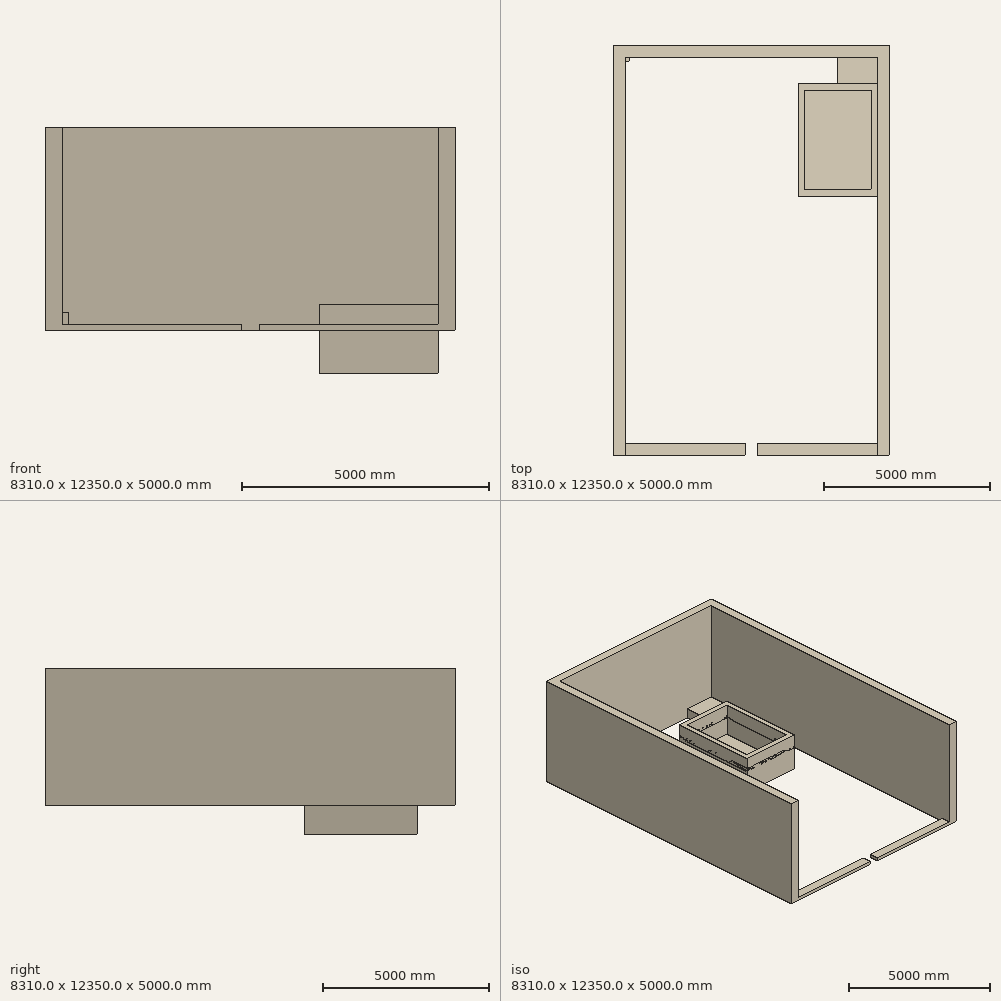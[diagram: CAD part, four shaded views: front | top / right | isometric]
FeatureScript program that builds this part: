
annotation { "Feature Type Name" : "Feature", "Feature Type Description" : "" }
export const myFeature = defineFeature(function(context is Context, id is Id, definition is map)
    precondition{}
    {
        {
            var Q0;
            Q0=qCreatedBy(makeId("Top.planeOp"),FACE);
            var sketch = newSketch(context, id + "F0", { "sketchPlane" : qUnion([Q0])});
            skLineSegment(sketch, "E0.bottom", {"start": v(-3805, 5655) * mm, "end": v(3805, 5655) * mm});
            skLineSegment(sketch, "E0.top", {"start": v(-3805, -5655) * mm, "end": v(3805, -5655) * mm});
            skLineSegment(sketch, "E0.left", {"start": v(-3805, 5655) * mm, "end": v(-3805, -5655) * mm});
            skLineSegment(sketch, "E0.right", {"start": v(3805, 5655) * mm, "end": v(3805, -5655) * mm});
            skPoint(sketch, "E0.middle", {"position": v(0, 0) * mm});
            skLineSegment(sketch, "E1.top", {"start": v(-3805, -5995) * mm, "end": v(3805, -5995) * mm});
            skLineSegment(sketch, "E1.left", {"start": v(-3805, -5655) * mm, "end": v(-3805, -5995) * mm});
            skLineSegment(sketch, "E1.right", {"start": v(3805, -5655) * mm, "end": v(3805, -5995) * mm});
            skLineSegment(sketch, "E2.bottom", {"start": v(-3805, 5655) * mm, "end": v(-3685, 5655) * mm});
            skLineSegment(sketch, "E2.top", {"start": v(-3805, 5535) * mm, "end": v(-3685, 5535) * mm});
            skLineSegment(sketch, "E2.left", {"start": v(-3805, 5655) * mm, "end": v(-3805, 5535) * mm});
            skLineSegment(sketch, "E2.right", {"start": v(-3685, 5655) * mm, "end": v(-3685, 5535) * mm});
            skLineSegment(sketch, "E3.bottom", {"start": v(3805, 5655) * mm, "end": v(2605, 5655) * mm});
            skLineSegment(sketch, "E3.top", {"start": v(3805, 4855) * mm, "end": v(2605, 4855) * mm});
            skLineSegment(sketch, "E3.left", {"start": v(3805, 5655) * mm, "end": v(3805, 4855) * mm});
            skLineSegment(sketch, "E3.right", {"start": v(2605, 5655) * mm, "end": v(2605, 4855) * mm});
            skLineSegment(sketch, "E4.bottom", {"start": v(3805, 4855) * mm, "end": v(1405, 4855) * mm});
            skLineSegment(sketch, "E4.top", {"start": v(3805, 1455) * mm, "end": v(1405, 1455) * mm});
            skLineSegment(sketch, "E4.left", {"start": v(3805, 4855) * mm, "end": v(3805, 1455) * mm});
            skLineSegment(sketch, "E4.right", {"start": v(1405, 4855) * mm, "end": v(1405, 1455) * mm});
            skPoint(sketch, "E4.middle", {"position": v(2605, 3155) * mm});
            skLineSegment(sketch, "E5.0", {"start": v(3605, 4655) * mm, "end": v(3605, 1655) * mm});
            skLineSegment(sketch, "E5.1", {"start": v(3605, 4655) * mm, "end": v(1605, 4655) * mm});
            skLineSegment(sketch, "E5.2", {"start": v(1605, 4655) * mm, "end": v(1605, 1655) * mm});
            skLineSegment(sketch, "E5.3", {"start": v(3605, 1655) * mm, "end": v(1605, 1655) * mm});
            skLineSegment(sketch, "E6", {"start": v(1405, 3595) * mm, "end": v(-3805, 3595) * mm});
            skLineSegment(sketch, "E7.0", {"start": v(-4155, 6005) * mm, "end": v(-4155, -5655) * mm});
            skLineSegment(sketch, "E7.1", {"start": v(4155, 6005) * mm, "end": v(4155, -5655) * mm});
            skLineSegment(sketch, "E7.2", {"start": v(4155, -5655) * mm, "end": v(4155, -6345) * mm});
            skLineSegment(sketch, "E7.3", {"start": v(-4155, 6005) * mm, "end": v(4155, 6005) * mm});
            skLineSegment(sketch, "E7.4", {"start": v(-4155, -6345) * mm, "end": v(4155, -6345) * mm});
            skLineSegment(sketch, "E7.5", {"start": v(-4155, -5655) * mm, "end": v(-4155, -6345) * mm});
            skLineSegment(sketch, "E8.bottom", {"start": v(175, -5995) * mm, "end": v(-175, -5995) * mm});
            skLineSegment(sketch, "E8.top", {"start": v(175, -6345) * mm, "end": v(-175, -6345) * mm});
            skLineSegment(sketch, "E8.left", {"start": v(175, -5995) * mm, "end": v(175, -6345) * mm});
            skLineSegment(sketch, "E8.right", {"start": v(-175, -5995) * mm, "end": v(-175, -6345) * mm});
            skPoint(sketch, "E8.middle", {"position": v(0, -6170) * mm});
            skLineSegment(sketch, "E9", {"start": v(-3805, -5995) * mm, "end": v(-3805, -6345) * mm});
            skLineSegment(sketch, "E10", {"start": v(3805, -5995) * mm, "end": v(3805, -6345) * mm});
            skSolve(sketch);
        }
        {
            var Q0;
            {var subQ2=sQuery(id+"F0.wireOp",EDGE,"E8.right");Q0=makeQuery(id+"F0.imprint","IMPRINT",FACE,{"disambiguationData":[TD([[makeQuery(id+"F0.imprint","IMPRINT",EDGE,{"derivedFrom":subQ2}),-1.0]])]});}
            var Q1;
            {var subQ2=sQuery(id+"F0.wireOp",EDGE,"E8.left");Q1=makeQuery(id+"F0.imprint","IMPRINT",FACE,{"disambiguationData":[TD([[makeQuery(id+"F0.imprint","IMPRINT",EDGE,{"derivedFrom":subQ2}),1.0]])]});}
            var Q2;
            Q2=makeQuery(id+"F0.imprint","IMPRINT",FACE,{"disambiguationData":[TD([[makeQuery(id+"F0.imprint","IMPRINT",EDGE,{"derivedFrom":sQuery(id+"F0.wireOp",EDGE,"E3.bottom")}),1.0]])]});
            var Q3;
            Q3=makeQuery(id+"F0.imprint","IMPRINT",FACE,{"disambiguationData":[TD([[makeQuery(id+"F0.imprint","IMPRINT",EDGE,{"derivedFrom":sQuery(id+"F0.wireOp",EDGE,"E0.right")}),-1.0]])]});
            var Q4;
            Q4=makeQuery(id+"F0.imprint","IMPRINT",FACE,{"disambiguationData":[TD([[makeQuery(id+"F0.imprint","IMPRINT",EDGE,{"derivedFrom":sQuery(id+"F0.wireOp",EDGE,"E0.bottom")}),-1.0]])]});
            var Q5;
            {var subQ1=sQuery(id+"F0.wireOp",EDGE,"E4.top");Q5=makeQuery(id+"F0.imprint","IMPRINT",FACE,{"disambiguationData":[TD([[makeQuery(id+"F0.imprint","IMPRINT",EDGE,{"derivedFrom":subQ1}),-1.0]])]});}
            var Q6;
            Q6=makeQuery(id+"F0.imprint","IMPRINT",FACE,{"disambiguationData":[TD([[makeQuery(id+"F0.imprint","IMPRINT",EDGE,{"derivedFrom":sQuery(id+"F0.wireOp",EDGE,"E0.bottom")}),1.0]])]});
            var Q7;
            Q7=makeQuery(id+"F0.imprint","IMPRINT",FACE,{"disambiguationData":[TD([[makeQuery(id+"F0.imprint","IMPRINT",EDGE,{"derivedFrom":sQuery(id+"F0.wireOp",EDGE,"E8.bottom")}),1.0]])]});
            var Q8;
            Q8=makeQuery(id+"F0.imprint","IMPRINT",FACE,{"disambiguationData":[TD([[makeQuery(id+"F0.imprint","IMPRINT",EDGE,{"derivedFrom":sQuery(id+"F0.wireOp",EDGE,"E2.bottom")}),-1.0]])]});
            extrude(context, id + "F1", {"entities" : qUnion([Q0, Q1, Q2, Q3, Q4, Q5, Q6, Q7, Q8]), "oppositeDirection" : true, "depth" : 130 * mm});
        }
        {
            var Q0;
            Q0=makeQuery(id+"F0.imprint","IMPRINT",FACE,{"disambiguationData":[TD([[makeQuery(id+"F0.imprint","IMPRINT",EDGE,{"derivedFrom":sQuery(id+"F0.wireOp",EDGE,"E0.bottom")}),-1.0]])]});
            var Q1;
            Q1=makeQuery(id+"F0.imprint","IMPRINT",FACE,{"disambiguationData":[TD([[makeQuery(id+"F0.imprint","IMPRINT",EDGE,{"derivedFrom":sQuery(id+"F0.wireOp",EDGE,"E3.bottom")}),1.0]])]});
            extrude(context, id + "F2", {"entities" : qUnion([Q0, Q1]), "operationType" : NewBodyOperationType.ADD, "depth" : 250 * mm});
        }
        {
            var Q0;
            Q0=makeQuery(id+"F0.imprint","IMPRINT",FACE,{"disambiguationData":[TD([[makeQuery(id+"F0.imprint","IMPRINT",EDGE,{"derivedFrom":sQuery(id+"F0.wireOp",EDGE,"E0.bottom")}),1.0]])]});
            var Q1;
            Q1=makeQuery(id+"F0.imprint","IMPRINT",FACE,{"disambiguationData":[TD([[makeQuery(id+"F0.imprint","IMPRINT",EDGE,{"derivedFrom":sQuery(id+"F0.wireOp",EDGE,"E8.bottom")}),1.0]])]});
            var Q2;
            Q2=makeQuery(id+"F0.imprint","IMPRINT",FACE,{"disambiguationData":[TD([[makeQuery(id+"F0.imprint","IMPRINT",EDGE,{"derivedFrom":sQuery(id+"F0.wireOp",EDGE,"E2.bottom")}),-1.0]])]});
            extrude(context, id + "F3", {"entities" : qUnion([Q0, Q1, Q2]), "operationType" : NewBodyOperationType.ADD, "depth" : 4000 * mm});
        }
        {
            var Q0;
            {var subQ1=sQuery(id+"F0.wireOp",EDGE,"E4.top");Q0=makeQuery(id+"F0.imprint","IMPRINT",FACE,{"disambiguationData":[TD([[makeQuery(id+"F0.imprint","IMPRINT",EDGE,{"derivedFrom":subQ1}),-1.0]])]});}
            extrude(context, id + "F4", {"entities" : qUnion([Q0]), "operationType" : NewBodyOperationType.ADD, "depth" : 400 * mm});
        }
        {
            var Q0;
            {var subQ1=sQuery(id+"F0.wireOp",EDGE,"E4.top");Q0=makeQuery(id+"F0.imprint","IMPRINT",FACE,{"disambiguationData":[TD([[makeQuery(id+"F0.imprint","IMPRINT",EDGE,{"derivedFrom":subQ1}),-1.0]])]});}
            var Q1;
            Q1=makeQuery(id+"F0.imprint","IMPRINT",FACE,{"disambiguationData":[TD([[makeQuery(id+"F0.imprint","IMPRINT",EDGE,{"derivedFrom":sQuery(id+"F0.wireOp",EDGE,"E5.0")}),-1.0]])]});
            extrude(context, id + "F5", {"entities" : qUnion([Q0, Q1]), "oppositeDirection" : true, "depth" : 1000 * mm});
        }
        {
            var Q0;
            Q0=makeQuery(id+"F5.opExtrude","CAP_FACE",FACE,{"disambiguationData":[OSD([sQuery(id+"F0.wireOp",EDGE,"E4.bottom"),sQuery(id+"F0.wireOp",EDGE,"E4.top"),sQuery(id+"F0.wireOp",EDGE,"E4.left"),sQuery(id+"F0.wireOp",EDGE,"E4.right")])],"isStart":true});
            shell(context, id + "F6", {"entities" : qUnion([Q0]), "thickness" : 200 * mm});
        }
    });
